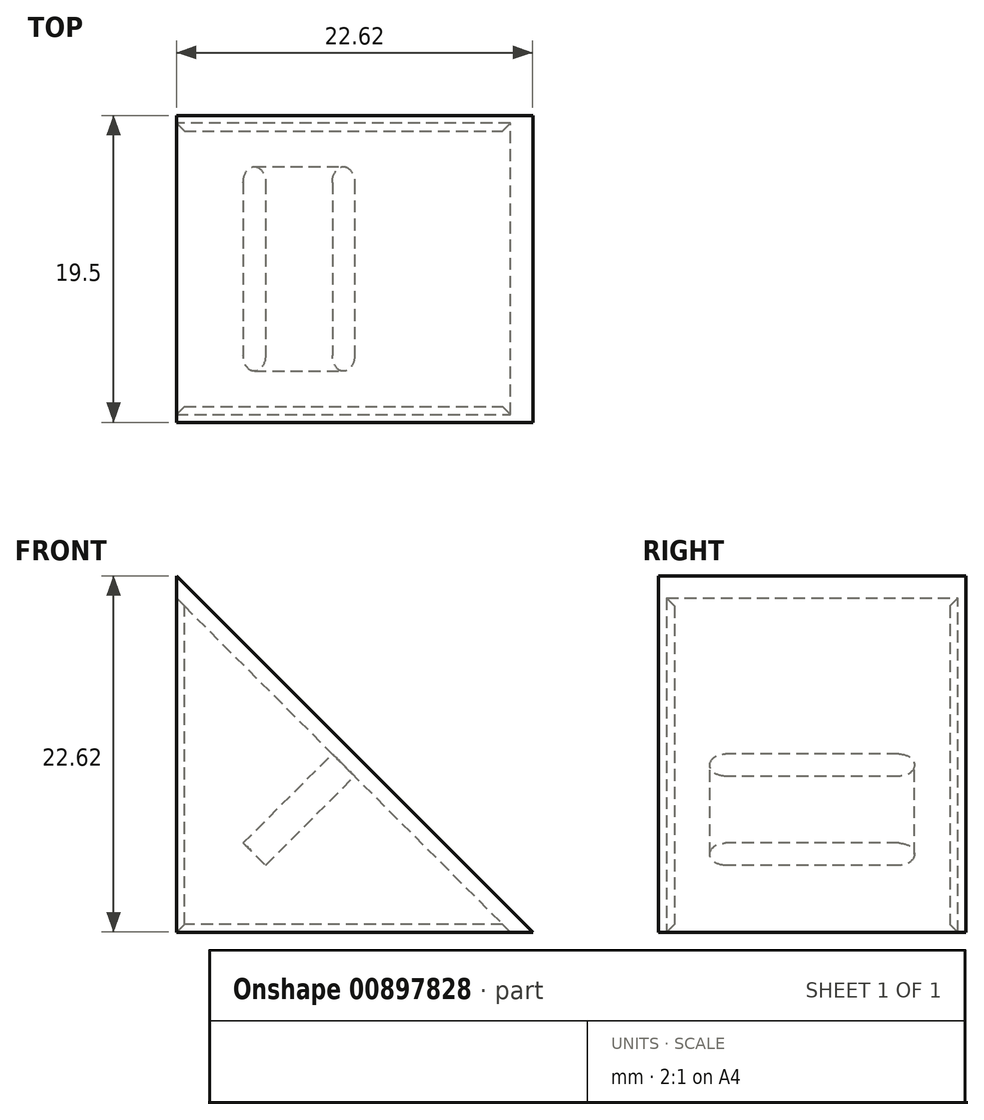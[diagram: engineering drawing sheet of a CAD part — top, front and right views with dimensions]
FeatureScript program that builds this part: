
annotation { "Feature Type Name" : "Feature", "Feature Type Description" : "" }
export const myFeature = defineFeature(function(context is Context, id is Id, definition is map)
    precondition{}
    {
        {
            var Q0;
            Q0=qCreatedBy(makeId("Front.planeOp"),FACE);
            var sketch = newSketch(context, id + "F0", { "sketchPlane" : qUnion([Q0])});
            skLineSegment(sketch, "E0.bottom", {"start": v(-11.31, -11.31) * mm, "end": v(11.31, -11.31) * mm});
            skLineSegment(sketch, "E0.left", {"start": v(-11.31, -11.31) * mm, "end": v(-11.31, 11.31) * mm});
            skPoint(sketch, "E0.middle", {"position": v(0, 0) * mm});
            skLineSegment(sketch, "E1", {"start": v(-11.31, 11.31) * mm, "end": v(11.31, -11.31) * mm});
            skSolve(sketch);
        }
        {
            var Q0;
            Q0=makeQuery(id+"F0.imprint","IMPRINT",FACE,{"disambiguationData":[TD([[makeQuery(id+"F0.imprint","IMPRINT",EDGE,{"derivedFrom":sQuery(id+"F0.wireOp",EDGE,"E0.bottom")}),1.0]])]});
            extrude(context, id + "F1", {"entities" : qUnion([Q0]), "depth" : 19.5 * mm, "offsetDistance" : 25 * mm});
        }
        {
            var Q0;
            Q0=makeQuery(id+"F1.opExtrude","SWEPT_FACE",FACE,{"disambiguationData":[OSD([sQuery(id+"F0.wireOp",EDGE,"E0.bottom")])]});
            var Q1;
            Q1=makeQuery(id+"F1.opExtrude","SWEPT_FACE",FACE,{"disambiguationData":[OSD([sQuery(id+"F0.wireOp",EDGE,"E0.left")])]});
            shell(context, id + "F2", {"entities" : qUnion([Q0, Q1]), "thickness" : 1 * mm});
        }
        {
            var Q0;
            Q0=makeQuery(id+"F2.opShell","OFFSET_FACE",FACE,{"disambiguationData":[OSD([sQuery(id+"F0.wireOp",EDGE,"E1")])]});
            var sketch = newSketch(context, id + "F3", { "sketchPlane" : qUnion([Q0])});
            skPoint(sketch, "E2", {"position": v(16.25, 0) * mm});
            skLineSegment(sketch, "E3.bottom", {"start": v(4.25, 1) * mm, "end": v(15.25, 1) * mm});
            skLineSegment(sketch, "E3.top", {"start": v(4.25, -1) * mm, "end": v(15.25, -1) * mm});
            skLineSegment(sketch, "E3.left", {"start": v(3.25, 0) * mm, "end": v(3.25, 0) * mm});
            skLineSegment(sketch, "E3.right", {"start": v(16.25, 0) * mm, "end": v(16.25, 0) * mm});
            skPoint(sketch, "E3.middle", {"position": v(9.75, 0) * mm});
            skPoint(sketch, "E4.orphan", {"position": v(18.5, 0) * mm});
            skPoint(sketch, "E5.orphan", {"position": v(1, 0) * mm});
            skPoint(sketch, "E6.visualSharp", {"position": v(3.25, 1) * mm});
            skArc(sketch, "E6.filletArc", {"start": v(4.25, 1) * mm, "mid": v(3.54, 0.7) * mm, "end": v(3.25, 0) * mm});
            skPoint(sketch, "E7.visualSharp", {"position": v(3.25, -1) * mm});
            skArc(sketch, "E7.filletArc", {"start": v(3.25, 0) * mm, "mid": v(3.54, -0.7) * mm, "end": v(4.25, -1) * mm});
            skPoint(sketch, "E8.visualSharp", {"position": v(16.25, -1) * mm});
            skArc(sketch, "E8.filletArc", {"start": v(15.25, -1) * mm, "mid": v(15.96, -0.7) * mm, "end": v(16.25, 0) * mm});
            skPoint(sketch, "E9.visualSharp", {"position": v(16.25, 1) * mm});
            skArc(sketch, "E9.filletArc", {"start": v(16.25, 0) * mm, "mid": v(15.96, 0.7) * mm, "end": v(15.25, 1) * mm});
            skSolve(sketch);
        }
        {
            var Q0;
            Q0=makeQuery(id+"F3.imprint","IMPRINT",FACE,{"disambiguationData":[TD([[makeQuery(id+"F3.imprint","IMPRINT",EDGE,{"derivedFrom":sQuery(id+"F3.wireOp",EDGE,"E3.bottom")}),-1.0]])]});
            extrude(context, id + "F4", {"entities" : qUnion([Q0]), "operationType" : NewBodyOperationType.ADD, "depth" : 8 * mm, "offsetDistance" : 25 * mm});
        }
        {
            var Q0;
            {var subQ0=sQuery(id+"F0.wireOp",EDGE,"E0.bottom");Q0=makeQuery(id+"F2.opShell","OFFSET_EDGE",EDGE,{"disambiguationData":[OSD([subQ0]),TDD([makeQuery(id+"F1.opExtrude","CAP_EDGE",EDGE,{"disambiguationData":[OSD([subQ0])],"isStart":true})])]});}
            var Q1;
            {var subQ0=sQuery(id+"F0.wireOp",EDGE,"E0.left");Q1=makeQuery(id+"F2.opShell","OFFSET_EDGE",EDGE,{"disambiguationData":[OSD([subQ0]),TDD([makeQuery(id+"F1.opExtrude","CAP_EDGE",EDGE,{"disambiguationData":[OSD([subQ0])],"isStart":true})])]});}
            var Q2;
            {var subQ0=sQuery(id+"F0.wireOp",EDGE,"E0.left");Q2=makeQuery(id+"F2.opShell","OFFSET_EDGE",EDGE,{"disambiguationData":[OSD([subQ0]),TDD([makeQuery(id+"F1.opExtrude","CAP_EDGE",EDGE,{"disambiguationData":[OSD([subQ0])],"isStart":false})])]});}
            var Q3;
            {var subQ0=sQuery(id+"F0.wireOp",EDGE,"E0.bottom");Q3=makeQuery(id+"F2.opShell","OFFSET_EDGE",EDGE,{"disambiguationData":[OSD([subQ0]),TDD([makeQuery(id+"F1.opExtrude","CAP_EDGE",EDGE,{"disambiguationData":[OSD([subQ0])],"isStart":false})])]});}
            chamfer(context, id + "F5", {"entities" : qUnion([Q0, Q1, Q2, Q3]), "width" : .5 * mm, "tangentPropagation" : true});
        }
    });
